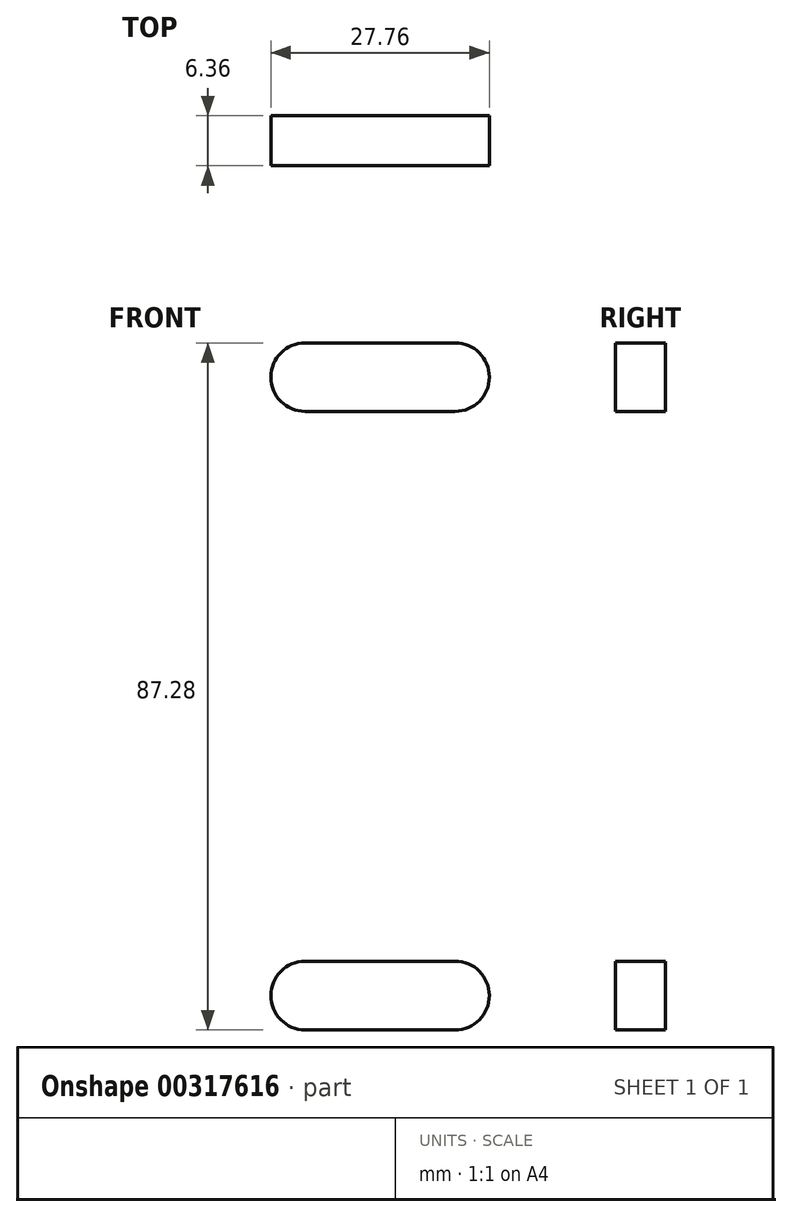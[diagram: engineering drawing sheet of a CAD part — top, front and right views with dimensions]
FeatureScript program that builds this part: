
annotation { "Feature Type Name" : "Feature", "Feature Type Description" : "" }
export const myFeature = defineFeature(function(context is Context, id is Id, definition is map)
    precondition{}
    {
        {
            var Q0;
            Q0=qCreatedBy(makeId("Front.planeOp"),FACE);
            var sketch = newSketch(context, id + "F0", { "sketchPlane" : qUnion([Q0])});
            skLineSegment(sketch, "E0.bottom", {"start": v(-101.6, 63.5) * mm, "end": v(101.6, 63.5) * mm});
            skLineSegment(sketch, "E0.top", {"start": v(-101.6, -63.5) * mm, "end": v(101.6, -63.5) * mm});
            skLineSegment(sketch, "E0.left", {"start": v(-101.6, 63.5) * mm, "end": v(-101.6, -63.5) * mm});
            skLineSegment(sketch, "E0.right", {"start": v(101.6, 63.5) * mm, "end": v(101.6, -63.5) * mm});
            skPoint(sketch, "E0.middle", {"position": v(0, 0) * mm});
            skSolve(sketch);
        }
        {
            var Q0;
            Q0=makeQuery(id+"F0.imprint","IMPRINT",FACE,{"disambiguationData":[TD([[makeQuery(id+"F0.imprint","IMPRINT",EDGE,{"derivedFrom":sQuery(id+"F0.wireOp",EDGE,"E0.bottom")}),-1.0]])]});
            extrude(context, id + "F1", {"entities" : qUnion([Q0]), "endBound" : BoundingType.SYMMETRIC, "depth" : 6.35 * mm});
        }
        {
            var Q0;
            Q0=makeQuery(id+"F1.opExtrude","CAP_FACE",FACE,{"disambiguationData":[OSD([sQuery(id+"F0.wireOp",EDGE,"E0.bottom"),sQuery(id+"F0.wireOp",EDGE,"E0.top"),sQuery(id+"F0.wireOp",EDGE,"E0.left"),sQuery(id+"F0.wireOp",EDGE,"E0.right")])],"isStart":false});
            var sketch = newSketch(context, id + "F2", { "sketchPlane" : qUnion([Q0])});
            skLineSegment(sketch, "E1", {"start": v(-61.5, 47.62) * mm, "end": v(-61.5, 28.57) * mm});
            skLineSegment(sketch, "E2", {"start": v(-52.8, 47.62) * mm, "end": v(-52.8, 28.57) * mm});
            skLineSegment(sketch, "E3", {"start": v(-61.5, -30.94) * mm, "end": v(-61.5, -49.99) * mm});
            skLineSegment(sketch, "E4", {"start": v(-52.8, -30.94) * mm, "end": v(-52.8, -49.99) * mm});
            skArc(sketch, "E5", {"start": v(-52.8, -30.94) * mm, "mid": v(-57.15, -26.58) * mm, "end": v(-61.5, -30.94) * mm});
            skArc(sketch, "E6", {"start": v(-61.5, -49.99) * mm, "mid": v(-57.15, -54.34) * mm, "end": v(-52.8, -49.99) * mm});
            skArc(sketch, "E7", {"start": v(-52.8, 28.57) * mm, "mid": v(-57.15, 24.22) * mm, "end": v(-61.5, 28.57) * mm});
            skArc(sketch, "E8", {"start": v(-52.8, 47.62) * mm, "mid": v(-57.15, 51.98) * mm, "end": v(-61.5, 47.62) * mm});
            skLineSegment(sketch, "E9", {"start": v(66.68, 38.1) * mm, "end": v(85.73, 38.1) * mm});
            skLineSegment(sketch, "E10", {"start": v(66.67, -40.46) * mm, "end": v(85.72, -40.46) * mm});
            skArc(sketch, "E11.0.startCap", {"start": v(66.67, -44.82) * mm, "mid": v(62.32, -40.46) * mm, "end": v(66.67, -36.1) * mm});
            skArc(sketch, "E11.0.endCap", {"start": v(85.72, -36.1) * mm, "mid": v(90.08, -40.46) * mm, "end": v(85.72, -44.82) * mm});
            skLineSegment(sketch, "E11.0.left", {"start": v(66.67, -36.1) * mm, "end": v(85.72, -36.1) * mm});
            skLineSegment(sketch, "E11.0.right", {"start": v(66.67, -44.82) * mm, "end": v(85.72, -44.82) * mm});
            skArc(sketch, "E12.0.startCap", {"start": v(66.68, 33.74) * mm, "mid": v(62.32, 38.1) * mm, "end": v(66.68, 42.46) * mm});
            skArc(sketch, "E12.0.endCap", {"start": v(85.73, 42.46) * mm, "mid": v(90.08, 38.1) * mm, "end": v(85.73, 33.74) * mm});
            skLineSegment(sketch, "E12.0.left", {"start": v(66.68, 42.46) * mm, "end": v(85.73, 42.46) * mm});
            skLineSegment(sketch, "E12.0.right", {"start": v(66.68, 33.74) * mm, "end": v(85.73, 33.74) * mm});
            skSolve(sketch);
        }
        {
            var Q0;
            Q0=makeQuery(id+"F2.imprint","IMPRINT",FACE,{"disambiguationData":[TD([[makeQuery(id+"F2.imprint","IMPRINT",EDGE,{"derivedFrom":sQuery(id+"F2.wireOp",EDGE,"E1")}),1.0]])]});
            var Q1;
            Q1=makeQuery(id+"F2.imprint","IMPRINT",FACE,{"disambiguationData":[TD([[makeQuery(id+"F2.imprint","IMPRINT",EDGE,{"derivedFrom":sQuery(id+"F2.wireOp",EDGE,"E3")}),1.0]])]});
            var Q2;
            Q2=makeQuery(id+"F2.imprint","IMPRINT",FACE,{"disambiguationData":[TD([[makeQuery(id+"F2.imprint","IMPRINT",EDGE,{"derivedFrom":sQuery(id+"F2.wireOp",EDGE,"E12.0.startCap")}),-1.0]])]});
            var Q3;
            Q3=makeQuery(id+"F2.imprint","IMPRINT",FACE,{"disambiguationData":[TD([[makeQuery(id+"F2.imprint","IMPRINT",EDGE,{"derivedFrom":sQuery(id+"F2.wireOp",EDGE,"E11.0.startCap")}),-1.0]])]});
            extrude(context, id + "F3", {"entities" : qUnion([Q0, Q1, Q2, Q3]), "operationType" : NewBodyOperationType.REMOVE, "oppositeDirection" : true, "depth" : 25.4 * mm});
        }
    });
